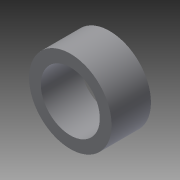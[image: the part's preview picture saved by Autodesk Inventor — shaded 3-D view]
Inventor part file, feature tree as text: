
AUTODESK INVENTOR PART (.ipt)
format: ipt  version: 2013 (Build 170138000, 138)  size: 78,336 bytes
history: native  units: mm
features: other x1, extrude x1, sketch x1
ambient origin geometry x8: Origin, YZ Plane, XZ Plane, XY Plane, X Axis, Y Axis, Z Axis, Center Point
feature tree (3):
  other  "ソリッド1"
  extrude  "押し出し1"  Depth=21.0mm
  sketch  "スケッチ1"
